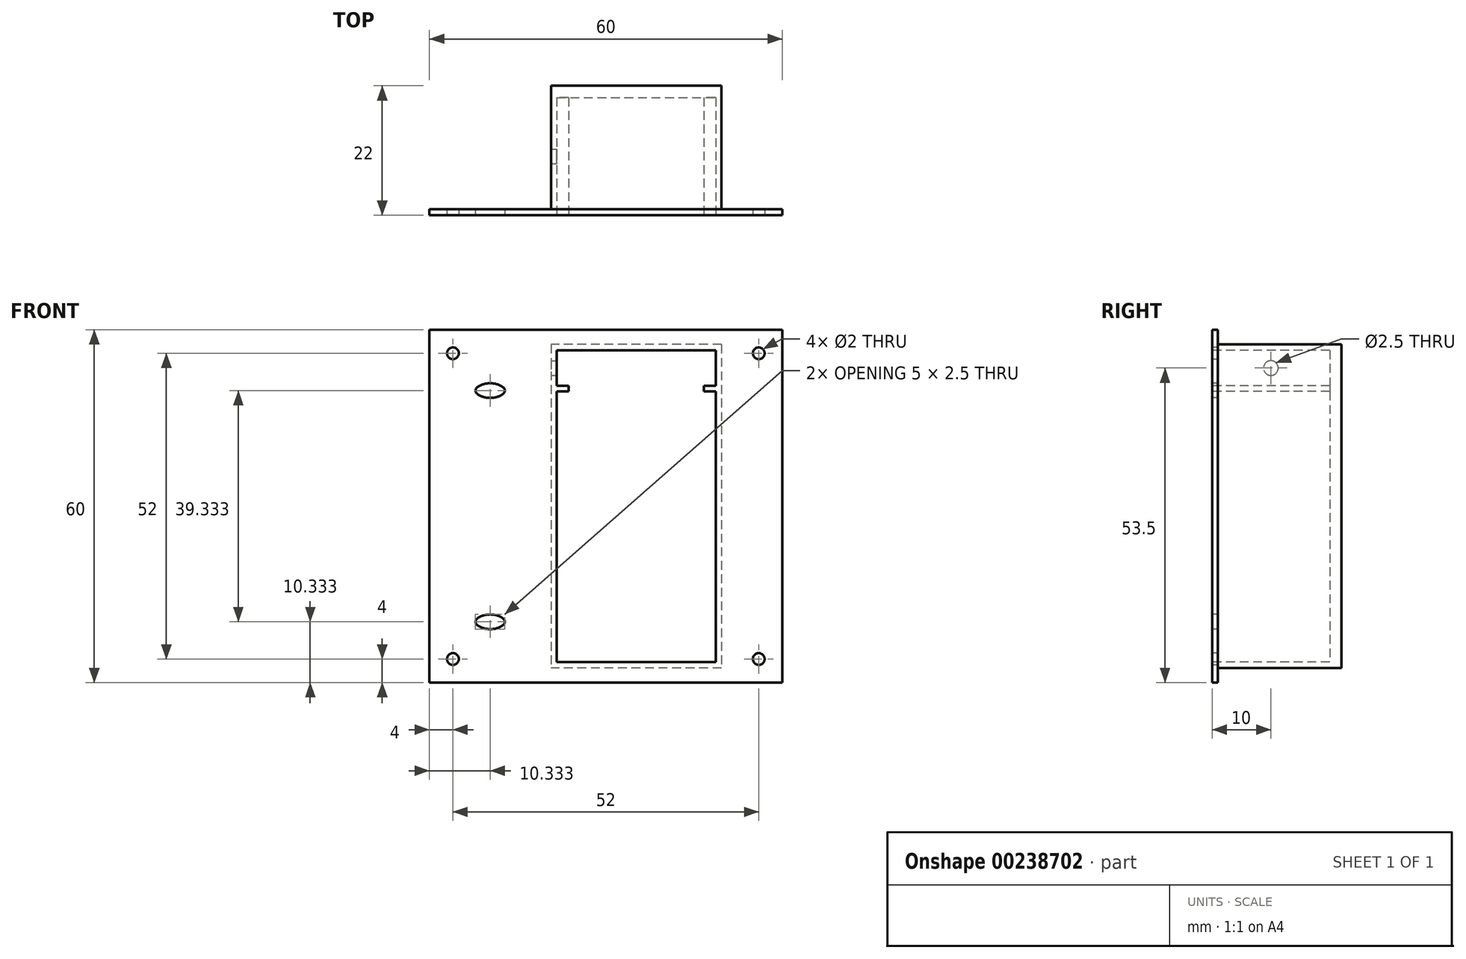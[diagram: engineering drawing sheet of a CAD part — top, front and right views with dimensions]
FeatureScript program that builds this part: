
annotation { "Feature Type Name" : "Feature", "Feature Type Description" : "" }
export const myFeature = defineFeature(function(context is Context, id is Id, definition is map)
    precondition{}
    {
        {
            var Q0;
            Q0=qCreatedBy(makeId("Front.planeOp"),FACE);
            var sketch = newSketch(context, id + "F0", { "sketchPlane" : qUnion([Q0])});
            skCircle(sketch, "E0", {"center": v(26.5, 16.25) * mm, "radius": 6.5 * mm, "construction": true});
            skCircle(sketch, "E1", {"center": v(45.5, 9.5) * mm, "radius": 4.5 * mm});
            skCircle(sketch, "E2", {"center": v(45.5, 9.5) * mm, "radius": 3 * mm});
            skCircle(sketch, "E3", {"center": v(45.5, 24.5) * mm, "radius": 3 * mm});
            skCircle(sketch, "E4", {"center": v(45.5, 24.5) * mm, "radius": 2.5 * mm});
            skLineSegment(sketch, "E5", {"start": v(45.5, 27.5) * mm, "end": v(45.5, 5) * mm, "construction": true});
            skPoint(sketch, "E6.positionSnap0", {"position": v(45.5, 16.25) * mm});
            skLineSegment(sketch, "E7.bottom", {"start": v(15, 32.5) * mm, "end": v(55, 32.5) * mm});
            skLineSegment(sketch, "E7.top", {"start": v(15, 0) * mm, "end": v(55, 0) * mm});
            skLineSegment(sketch, "E7.left", {"start": v(15, 32.5) * mm, "end": v(15, 0) * mm});
            skLineSegment(sketch, "E7.right", {"start": v(55, 32.5) * mm, "end": v(55, 0) * mm});
            skLineSegment(sketch, "E8", {"start": v(20.5, 22.25) * mm, "end": v(20.5, 23.75) * mm});
            skLineSegment(sketch, "E9", {"start": v(20.5, 23.75) * mm, "end": v(32.5, 23.75) * mm});
            skLineSegment(sketch, "E10", {"start": v(32.5, 23.75) * mm, "end": v(32.5, 22.25) * mm});
            skLineSegment(sketch, "E11", {"start": v(15, 16.25) * mm, "end": v(55, 16.25) * mm, "construction": true});
            skLineSegment(sketch, "E12.MirrorCS", {"start": v(32.5, 8.75) * mm, "end": v(32.5, 10.25) * mm});
            skLineSegment(sketch, "E13.MirrorCS", {"start": v(20.5, 8.75) * mm, "end": v(32.5, 8.75) * mm});
            skLineSegment(sketch, "E14.MirrorCS", {"start": v(20.5, 10.25) * mm, "end": v(20.5, 8.75) * mm});
            skLineSegment(sketch, "E15", {"start": v(50, 9.5) * mm, "end": v(55, 9.5) * mm, "construction": true});
            skLineSegment(sketch, "E16", {"start": v(41, 9.5) * mm, "end": v(41, 16.25) * mm, "construction": true});
            skLineSegment(sketch, "E17.bottom", {"start": v(32.5, 22.25) * mm, "end": v(20.5, 22.25) * mm});
            skLineSegment(sketch, "E17.top", {"start": v(32.5, 10.25) * mm, "end": v(20.5, 10.25) * mm});
            skLineSegment(sketch, "E17.left", {"start": v(32.5, 22.25) * mm, "end": v(32.5, 10.25) * mm});
            skLineSegment(sketch, "E17.right", {"start": v(20.5, 22.25) * mm, "end": v(20.5, 10.25) * mm});
            skLineSegment(sketch, "E18.bottom", {"start": v(24.5, 18.25) * mm, "end": v(28.5, 18.25) * mm});
            skLineSegment(sketch, "E18.top", {"start": v(24.5, 14.25) * mm, "end": v(28.5, 14.25) * mm});
            skLineSegment(sketch, "E18.left", {"start": v(24.5, 18.25) * mm, "end": v(24.5, 14.25) * mm});
            skLineSegment(sketch, "E18.right", {"start": v(28.5, 18.25) * mm, "end": v(28.5, 14.25) * mm});
            skLineSegment(sketch, "E19.1.0.0", {"start": v(92.5, 22.25) * mm, "end": v(80.5, 22.25) * mm});
            skCircle(sketch, "E19.1.0.1", {"center": v(105.5, 24.5) * mm, "radius": 2.5 * mm});
            skCircle(sketch, "E19.1.0.3", {"center": v(86.5, 16.25) * mm, "radius": 6.5 * mm, "construction": true});
            skLineSegment(sketch, "E19.1.0.4", {"start": v(115, 32.5) * mm, "end": v(115, 0) * mm});
            skLineSegment(sketch, "E19.1.0.5", {"start": v(75, 32.5) * mm, "end": v(115, 32.5) * mm});
            skLineSegment(sketch, "E19.1.0.6", {"start": v(84.5, 18.25) * mm, "end": v(84.5, 14.25) * mm});
            skLineSegment(sketch, "E19.1.0.7", {"start": v(84.5, 18.25) * mm, "end": v(88.5, 18.25) * mm});
            skLineSegment(sketch, "E19.1.0.8", {"start": v(92.5, 10.25) * mm, "end": v(80.5, 10.25) * mm});
            skLineSegment(sketch, "E19.1.0.9", {"start": v(80.5, 23.75) * mm, "end": v(92.5, 23.75) * mm});
            skCircle(sketch, "E19.1.0.10", {"center": v(105.5, 9.5) * mm, "radius": 4.5 * mm});
            skLineSegment(sketch, "E19.1.0.11", {"start": v(88.5, 18.25) * mm, "end": v(88.5, 14.25) * mm});
            skPoint(sketch, "E19.1.0.13", {"position": v(86.5, 16.25) * mm});
            skLineSegment(sketch, "E19.1.0.14", {"start": v(75, 32.5) * mm, "end": v(75, 0) * mm});
            skLineSegment(sketch, "E19.1.0.15", {"start": v(80.5, 8.75) * mm, "end": v(92.5, 8.75) * mm});
            skCircle(sketch, "E19.1.0.16", {"center": v(105.5, 9.5) * mm, "radius": 3 * mm});
            skCircle(sketch, "E19.1.0.17", {"center": v(105.5, 24.5) * mm, "radius": 3 * mm});
            skLineSegment(sketch, "E19.1.0.18", {"start": v(80.5, 22.25) * mm, "end": v(80.5, 10.25) * mm});
            skLineSegment(sketch, "E19.1.0.19", {"start": v(92.5, 22.25) * mm, "end": v(92.5, 10.25) * mm});
            skLineSegment(sketch, "E19.1.0.20", {"start": v(75, 0) * mm, "end": v(115, 0) * mm});
            skLineSegment(sketch, "E19.1.0.22", {"start": v(84.5, 14.25) * mm, "end": v(88.5, 14.25) * mm});
            skPoint(sketch, "E19.1.0.23", {"position": v(86.5, 16.25) * mm});
            skLineSegment(sketch, "E19.1.0.24", {"start": v(92.5, 23.75) * mm, "end": v(92.5, 22.25) * mm});
            skLineSegment(sketch, "E19.1.0.25", {"start": v(80.5, 22.25) * mm, "end": v(80.5, 23.75) * mm});
            skLineSegment(sketch, "E19.1.0.26", {"start": v(80.5, 10.25) * mm, "end": v(80.5, 8.75) * mm});
            skLineSegment(sketch, "E19.1.0.27", {"start": v(92.5, 8.75) * mm, "end": v(92.5, 10.25) * mm});
            skLineSegment(sketch, "E19.2.0.0", {"start": v(152.5, 22.25) * mm, "end": v(140.5, 22.25) * mm});
            skCircle(sketch, "E19.2.0.1", {"center": v(165.5, 24.5) * mm, "radius": 2.5 * mm});
            skCircle(sketch, "E19.2.0.3", {"center": v(146.5, 16.25) * mm, "radius": 6.5 * mm, "construction": true});
            skLineSegment(sketch, "E19.2.0.4", {"start": v(175, 32.5) * mm, "end": v(175, 0) * mm});
            skLineSegment(sketch, "E19.2.0.5", {"start": v(135, 32.5) * mm, "end": v(175, 32.5) * mm});
            skLineSegment(sketch, "E19.2.0.6", {"start": v(144.5, 18.25) * mm, "end": v(144.5, 14.25) * mm});
            skLineSegment(sketch, "E19.2.0.7", {"start": v(144.5, 18.25) * mm, "end": v(148.5, 18.25) * mm});
            skLineSegment(sketch, "E19.2.0.8", {"start": v(152.5, 10.25) * mm, "end": v(140.5, 10.25) * mm});
            skLineSegment(sketch, "E19.2.0.9", {"start": v(140.5, 23.75) * mm, "end": v(152.5, 23.75) * mm});
            skCircle(sketch, "E19.2.0.10", {"center": v(165.5, 9.5) * mm, "radius": 4.5 * mm});
            skLineSegment(sketch, "E19.2.0.11", {"start": v(148.5, 18.25) * mm, "end": v(148.5, 14.25) * mm});
            skPoint(sketch, "E19.2.0.13", {"position": v(146.5, 16.25) * mm});
            skLineSegment(sketch, "E19.2.0.14", {"start": v(135, 32.5) * mm, "end": v(135, 0) * mm});
            skLineSegment(sketch, "E19.2.0.15", {"start": v(140.5, 8.75) * mm, "end": v(152.5, 8.75) * mm});
            skCircle(sketch, "E19.2.0.16", {"center": v(165.5, 9.5) * mm, "radius": 3 * mm});
            skCircle(sketch, "E19.2.0.17", {"center": v(165.5, 24.5) * mm, "radius": 3 * mm});
            skLineSegment(sketch, "E19.2.0.18", {"start": v(140.5, 22.25) * mm, "end": v(140.5, 10.25) * mm});
            skLineSegment(sketch, "E19.2.0.19", {"start": v(152.5, 22.25) * mm, "end": v(152.5, 10.25) * mm});
            skLineSegment(sketch, "E19.2.0.20", {"start": v(135, 0) * mm, "end": v(175, 0) * mm});
            skLineSegment(sketch, "E19.2.0.22", {"start": v(144.5, 14.25) * mm, "end": v(148.5, 14.25) * mm});
            skPoint(sketch, "E19.2.0.23", {"position": v(146.5, 16.25) * mm});
            skLineSegment(sketch, "E19.2.0.24", {"start": v(152.5, 23.75) * mm, "end": v(152.5, 22.25) * mm});
            skLineSegment(sketch, "E19.2.0.25", {"start": v(140.5, 22.25) * mm, "end": v(140.5, 23.75) * mm});
            skLineSegment(sketch, "E19.2.0.26", {"start": v(140.5, 10.25) * mm, "end": v(140.5, 8.75) * mm});
            skLineSegment(sketch, "E19.2.0.27", {"start": v(152.5, 8.75) * mm, "end": v(152.5, 10.25) * mm});
            skLineSegment(sketch, "E19.3.0.0", {"start": v(212.5, 22.25) * mm, "end": v(200.5, 22.25) * mm});
            skCircle(sketch, "E19.3.0.1", {"center": v(225.5, 24.5) * mm, "radius": 2.5 * mm});
            skCircle(sketch, "E19.3.0.3", {"center": v(206.5, 16.25) * mm, "radius": 6.5 * mm, "construction": true});
            skLineSegment(sketch, "E19.3.0.4", {"start": v(235, 32.5) * mm, "end": v(235, 0) * mm});
            skLineSegment(sketch, "E19.3.0.5", {"start": v(195, 32.5) * mm, "end": v(235, 32.5) * mm});
            skLineSegment(sketch, "E19.3.0.6", {"start": v(204.5, 18.25) * mm, "end": v(204.5, 14.25) * mm});
            skLineSegment(sketch, "E19.3.0.7", {"start": v(204.5, 18.25) * mm, "end": v(208.5, 18.25) * mm});
            skLineSegment(sketch, "E19.3.0.8", {"start": v(212.5, 10.25) * mm, "end": v(200.5, 10.25) * mm});
            skLineSegment(sketch, "E19.3.0.9", {"start": v(200.5, 23.75) * mm, "end": v(212.5, 23.75) * mm});
            skCircle(sketch, "E19.3.0.10", {"center": v(225.5, 9.5) * mm, "radius": 4.5 * mm});
            skLineSegment(sketch, "E19.3.0.11", {"start": v(208.5, 18.25) * mm, "end": v(208.5, 14.25) * mm});
            skPoint(sketch, "E19.3.0.13", {"position": v(206.5, 16.25) * mm});
            skLineSegment(sketch, "E19.3.0.14", {"start": v(195, 32.5) * mm, "end": v(195, 0) * mm});
            skLineSegment(sketch, "E19.3.0.15", {"start": v(200.5, 8.75) * mm, "end": v(212.5, 8.75) * mm});
            skCircle(sketch, "E19.3.0.16", {"center": v(225.5, 9.5) * mm, "radius": 3 * mm});
            skCircle(sketch, "E19.3.0.17", {"center": v(225.5, 24.5) * mm, "radius": 3 * mm});
            skLineSegment(sketch, "E19.3.0.18", {"start": v(200.5, 22.25) * mm, "end": v(200.5, 10.25) * mm});
            skLineSegment(sketch, "E19.3.0.19", {"start": v(212.5, 22.25) * mm, "end": v(212.5, 10.25) * mm});
            skLineSegment(sketch, "E19.3.0.20", {"start": v(195, 0) * mm, "end": v(235, 0) * mm});
            skLineSegment(sketch, "E19.3.0.22", {"start": v(204.5, 14.25) * mm, "end": v(208.5, 14.25) * mm});
            skPoint(sketch, "E19.3.0.23", {"position": v(206.5, 16.25) * mm});
            skLineSegment(sketch, "E19.3.0.24", {"start": v(212.5, 23.75) * mm, "end": v(212.5, 22.25) * mm});
            skLineSegment(sketch, "E19.3.0.25", {"start": v(200.5, 22.25) * mm, "end": v(200.5, 23.75) * mm});
            skLineSegment(sketch, "E19.3.0.26", {"start": v(200.5, 10.25) * mm, "end": v(200.5, 8.75) * mm});
            skLineSegment(sketch, "E19.3.0.27", {"start": v(212.5, 8.75) * mm, "end": v(212.5, 10.25) * mm});
            skLineSegment(sketch, "E19.direction1", {"start": v(15, 0) * mm, "end": v(75, 0) * mm, "construction": true});
            skLineSegment(sketch, "E20.bottom", {"start": v(0, -92.5) * mm, "end": v(250, -92.5) * mm, "construction": true});
            skLineSegment(sketch, "E20.top", {"start": v(0, 47.5) * mm, "end": v(250, 47.5) * mm, "construction": true});
            skLineSegment(sketch, "E20.right", {"start": v(250, -92.5) * mm, "end": v(250, 47.5) * mm, "construction": true});
            skLineSegment(sketch, "E21", {"start": v(115, 0) * mm, "end": v(135, 0) * mm, "construction": true});
            skLineSegment(sketch, "E22.bottom", {"start": v(144.5, -39.17) * mm, "end": v(98.5, -39.17) * mm});
            skLineSegment(sketch, "E22.top", {"start": v(144.5, -66.17) * mm, "end": v(98.5, -66.17) * mm});
            skLineSegment(sketch, "E22.right", {"start": v(98.5, -39.17) * mm, "end": v(98.5, -66.17) * mm});
            skLineSegment(sketch, "E23.bottom", {"start": v(151.5, -39.17) * mm, "end": v(145.5, -39.17) * mm});
            skLineSegment(sketch, "E23.top", {"start": v(151.5, -66.17) * mm, "end": v(145.5, -66.17) * mm});
            skLineSegment(sketch, "E23.left", {"start": v(151.5, -39.17) * mm, "end": v(151.5, -66.17) * mm});
            skLineSegment(sketch, "E24.bottom", {"start": v(152.5, -67.17) * mm, "end": v(97.5, -67.17) * mm});
            skLineSegment(sketch, "E24.top", {"start": v(152.5, -38.17) * mm, "end": v(97.5, -38.17) * mm});
            skLineSegment(sketch, "E24.left", {"start": v(152.5, -67.17) * mm, "end": v(152.5, -38.17) * mm});
            skLineSegment(sketch, "E24.right", {"start": v(97.5, -67.17) * mm, "end": v(97.5, -38.17) * mm});
            skLineSegment(sketch, "E25", {"start": v(145.5, -64.17) * mm, "end": v(144.5, -64.17) * mm});
            skLineSegment(sketch, "E26", {"start": v(145.5, -41.17) * mm, "end": v(144.5, -41.17) * mm});
            skLineSegment(sketch, "E27", {"start": v(145.5, -66.17) * mm, "end": v(145.5, -64.17) * mm});
            skLineSegment(sketch, "E28", {"start": v(144.5, -66.17) * mm, "end": v(144.5, -64.17) * mm});
            skLineSegment(sketch, "E29", {"start": v(145.5, -41.17) * mm, "end": v(145.5, -39.17) * mm});
            skLineSegment(sketch, "E30", {"start": v(144.5, -41.17) * mm, "end": v(144.5, -39.17) * mm});
            skLineSegment(sketch, "E31.bottom", {"start": v(95, -77.5) * mm, "end": v(95, -17.5) * mm});
            skLineSegment(sketch, "E31.top", {"start": v(155, -77.5) * mm, "end": v(155, -17.5) * mm});
            skLineSegment(sketch, "E31.left", {"start": v(95, -77.5) * mm, "end": v(155, -77.5) * mm});
            skLineSegment(sketch, "E31.right", {"start": v(95, -17.5) * mm, "end": v(155, -17.5) * mm});
            skLineSegment(sketch, "E32", {"start": v(125, -38.17) * mm, "end": v(125, -17.5) * mm, "construction": true});
            skLineSegment(sketch, "E33", {"start": v(97.5, -67.17) * mm, "end": v(97.5, -77.5) * mm, "construction": true});
            skLineSegment(sketch, "E34", {"start": v(125, 0) * mm, "end": v(125, -92.5) * mm, "construction": true});
            skLineSegment(sketch, "E35.1.0.0", {"start": v(175, -77.5) * mm, "end": v(175, -17.5) * mm});
            skLineSegment(sketch, "E35.1.0.1", {"start": v(235, -77.5) * mm, "end": v(235, -17.5) * mm});
            skLineSegment(sketch, "E35.1.0.2", {"start": v(232.5, -67.17) * mm, "end": v(177.5, -67.17) * mm});
            skLineSegment(sketch, "E35.1.0.3", {"start": v(232.5, -67.17) * mm, "end": v(232.5, -38.17) * mm});
            skLineSegment(sketch, "E35.1.0.4", {"start": v(175, -17.5) * mm, "end": v(235, -17.5) * mm});
            skLineSegment(sketch, "E35.1.0.5", {"start": v(178.5, -39.17) * mm, "end": v(178.5, -66.17) * mm});
            skLineSegment(sketch, "E35.1.0.9", {"start": v(224.5, -66.17) * mm, "end": v(178.5, -66.17) * mm});
            skLineSegment(sketch, "E35.1.0.10", {"start": v(205, -38.17) * mm, "end": v(205, -17.5) * mm, "construction": true});
            skLineSegment(sketch, "E35.1.0.11", {"start": v(177.5, -67.17) * mm, "end": v(177.5, -77.5) * mm, "construction": true});
            skLineSegment(sketch, "E35.1.0.12", {"start": v(232.5, -38.17) * mm, "end": v(177.5, -38.17) * mm});
            skLineSegment(sketch, "E35.1.0.14", {"start": v(224.5, -39.17) * mm, "end": v(178.5, -39.17) * mm});
            skLineSegment(sketch, "E35.1.0.17", {"start": v(175, -77.5) * mm, "end": v(235, -77.5) * mm});
            skLineSegment(sketch, "E35.1.0.18", {"start": v(231.5, -39.17) * mm, "end": v(231.5, -66.17) * mm});
            skLineSegment(sketch, "E35.1.0.19", {"start": v(177.5, -67.17) * mm, "end": v(177.5, -38.17) * mm});
            skLineSegment(sketch, "E35.1.0.23", {"start": v(224.5, -41.17) * mm, "end": v(224.5, -39.17) * mm});
            skLineSegment(sketch, "E35.1.0.24", {"start": v(231.5, -39.17) * mm, "end": v(225.5, -39.17) * mm});
            skLineSegment(sketch, "E35.1.0.25", {"start": v(225.5, -41.17) * mm, "end": v(225.5, -39.17) * mm});
            skLineSegment(sketch, "E35.1.0.26", {"start": v(231.5, -66.17) * mm, "end": v(225.5, -66.17) * mm});
            skLineSegment(sketch, "E35.1.0.27", {"start": v(225.5, -66.17) * mm, "end": v(225.5, -64.17) * mm});
            skLineSegment(sketch, "E35.1.0.28", {"start": v(225.5, -41.17) * mm, "end": v(224.5, -41.17) * mm});
            skLineSegment(sketch, "E35.1.0.29", {"start": v(224.5, -66.17) * mm, "end": v(224.5, -64.17) * mm});
            skLineSegment(sketch, "E35.1.0.30", {"start": v(225.5, -64.17) * mm, "end": v(224.5, -64.17) * mm});
            skLineSegment(sketch, "E35.direction1", {"start": v(95, -77.5) * mm, "end": v(175, -77.5) * mm, "construction": true});
            skLineSegment(sketch, "E36.bottom", {"start": v(36.67, -28) * mm, "end": v(36.67, -74) * mm});
            skLineSegment(sketch, "E36.top", {"start": v(63.67, -28) * mm, "end": v(63.67, -74) * mm});
            skLineSegment(sketch, "E36.right", {"start": v(36.67, -74) * mm, "end": v(63.67, -74) * mm});
            skLineSegment(sketch, "E37.bottom", {"start": v(36.67, -21) * mm, "end": v(36.67, -27) * mm});
            skLineSegment(sketch, "E37.top", {"start": v(63.67, -21) * mm, "end": v(63.67, -27) * mm});
            skLineSegment(sketch, "E37.left", {"start": v(36.67, -21) * mm, "end": v(63.67, -21) * mm});
            skLineSegment(sketch, "E38.bottom", {"start": v(64.67, -20) * mm, "end": v(64.67, -75) * mm});
            skLineSegment(sketch, "E38.top", {"start": v(35.67, -20) * mm, "end": v(35.67, -75) * mm});
            skLineSegment(sketch, "E38.left", {"start": v(64.67, -20) * mm, "end": v(35.67, -20) * mm});
            skLineSegment(sketch, "E38.right", {"start": v(64.67, -75) * mm, "end": v(35.67, -75) * mm});
            skLineSegment(sketch, "E39", {"start": v(61.67, -27) * mm, "end": v(61.67, -28) * mm});
            skLineSegment(sketch, "E40", {"start": v(38.67, -27) * mm, "end": v(38.67, -28) * mm});
            skLineSegment(sketch, "E41", {"start": v(63.67, -27) * mm, "end": v(61.67, -27) * mm});
            skLineSegment(sketch, "E42", {"start": v(63.67, -28) * mm, "end": v(61.67, -28) * mm});
            skLineSegment(sketch, "E43", {"start": v(38.67, -27) * mm, "end": v(36.67, -27) * mm});
            skLineSegment(sketch, "E44", {"start": v(38.67, -28) * mm, "end": v(36.67, -28) * mm});
            skLineSegment(sketch, "E45.bottom", {"start": v(75, -77.5) * mm, "end": v(15, -77.5) * mm});
            skLineSegment(sketch, "E45.top", {"start": v(75, -17.5) * mm, "end": v(15, -17.5) * mm});
            skLineSegment(sketch, "E45.left", {"start": v(75, -77.5) * mm, "end": v(75, -17.5) * mm});
            skLineSegment(sketch, "E45.right", {"start": v(15, -77.5) * mm, "end": v(15, -17.5) * mm});
            skLineSegment(sketch, "E46", {"start": v(25.33, -29.08) * mm, "end": v(15, -29.08) * mm, "construction": true});
            skLineSegment(sketch, "E47", {"start": v(64.67, -29.08) * mm, "end": v(75, -29.08) * mm, "construction": true});
            skLineSegment(sketch, "E48", {"start": v(25.33, -29.08) * mm, "end": v(35.67, -29.08) * mm, "construction": true});
            skCircle(sketch, "E49", {"center": v(19, 28.5) * mm, "radius": 1 * mm});
            skCircle(sketch, "E50", {"center": v(51, 28.5) * mm, "radius": 1 * mm});
            skCircle(sketch, "E51", {"center": v(51, 4) * mm, "radius": 1 * mm});
            skCircle(sketch, "E52", {"center": v(19, 4) * mm, "radius": 1 * mm});
            skCircle(sketch, "E53", {"center": v(19, -21.5) * mm, "radius": 1 * mm});
            skCircle(sketch, "E54", {"center": v(71, -21.5) * mm, "radius": 1 * mm});
            skCircle(sketch, "E55", {"center": v(19, -73.5) * mm, "radius": 1 * mm});
            skCircle(sketch, "E56", {"center": v(71, -73.5) * mm, "radius": 1 * mm});
            skCircle(sketch, "E57.1.0.0", {"center": v(79, 28.5) * mm, "radius": 1 * mm});
            skCircle(sketch, "E57.1.0.1", {"center": v(79, 4) * mm, "radius": 1 * mm});
            skCircle(sketch, "E57.1.0.2", {"center": v(111, 4) * mm, "radius": 1 * mm});
            skCircle(sketch, "E57.1.0.3", {"center": v(111, 28.5) * mm, "radius": 1 * mm});
            skCircle(sketch, "E57.2.0.0", {"center": v(139, 28.5) * mm, "radius": 1 * mm});
            skCircle(sketch, "E57.2.0.1", {"center": v(139, 4) * mm, "radius": 1 * mm});
            skCircle(sketch, "E57.2.0.2", {"center": v(171, 4) * mm, "radius": 1 * mm});
            skCircle(sketch, "E57.2.0.3", {"center": v(171, 28.5) * mm, "radius": 1 * mm});
            skCircle(sketch, "E57.3.0.0", {"center": v(199, 28.5) * mm, "radius": 1 * mm});
            skCircle(sketch, "E57.3.0.1", {"center": v(199, 4) * mm, "radius": 1 * mm});
            skCircle(sketch, "E57.3.0.2", {"center": v(231, 4) * mm, "radius": 1 * mm});
            skCircle(sketch, "E57.3.0.3", {"center": v(231, 28.5) * mm, "radius": 1 * mm});
            skLineSegment(sketch, "E57.direction1", {"start": v(19, 4) * mm, "end": v(79, 4) * mm, "construction": true});
            skCircle(sketch, "E58.1.0.0", {"center": v(99, -73.5) * mm, "radius": 1 * mm});
            skCircle(sketch, "E58.1.0.1", {"center": v(151, -73.5) * mm, "radius": 1 * mm});
            skCircle(sketch, "E58.1.0.2", {"center": v(151, -21.5) * mm, "radius": 1 * mm});
            skCircle(sketch, "E58.1.0.3", {"center": v(99, -21.5) * mm, "radius": 1 * mm});
            skCircle(sketch, "E58.2.0.0", {"center": v(179, -73.5) * mm, "radius": 1 * mm});
            skCircle(sketch, "E58.2.0.1", {"center": v(231, -73.5) * mm, "radius": 1 * mm});
            skCircle(sketch, "E58.2.0.2", {"center": v(231, -21.5) * mm, "radius": 1 * mm});
            skCircle(sketch, "E58.2.0.3", {"center": v(179, -21.5) * mm, "radius": 1 * mm});
            skLineSegment(sketch, "E58.direction1", {"start": v(19, -73.5) * mm, "end": v(99, -73.5) * mm, "construction": true});
            skPoint(sketch, "E59.middle", {"position": v(25.33, -27.83) * mm});
            skLineSegment(sketch, "E60", {"start": v(15, -47.5) * mm, "end": v(35.67, -47.5) * mm, "construction": true});
            skPoint(sketch, "E61.1.0.0", {"position": v(112.5, -27.83) * mm});
            skLineSegment(sketch, "E62", {"start": v(112.5, -26.58) * mm, "end": v(112.5, -27.83) * mm, "construction": true});
            skLineSegment(sketch, "E63.bottom", {"start": v(115, -29.08) * mm, "end": v(110, -29.08) * mm, "construction": true});
            skLineSegment(sketch, "E63.top", {"start": v(115, -26.58) * mm, "end": v(110, -26.58) * mm, "construction": true});
            skLineSegment(sketch, "E63.left", {"start": v(115, -29.08) * mm, "end": v(115, -26.58) * mm, "construction": true});
            skLineSegment(sketch, "E63.right", {"start": v(110, -29.08) * mm, "end": v(110, -26.58) * mm, "construction": true});
            skFitSpline(sketch, "E64", {"points": [v(110, -27.83) * mm, v(110.5, -27.13) * mm, v(112.5, -26.58) * mm], "startDerivative": vector(0, 1.91) * mm, "endDerivative": vector(3.95, 0) * mm});
            skLineSegment(sketch, "E65", {"start": v(110, -27.83) * mm, "end": v(112.5, -27.83) * mm, "construction": true});
            skFitSpline(sketch, "E66.MirrorCS", {"points": [v(115, -27.83) * mm, v(114.5, -27.13) * mm, v(112.5, -26.58) * mm], "startDerivative": vector(0, 1.91) * mm, "endDerivative": vector(-3.95, 0) * mm});
            skFitSpline(sketch, "E67.MirrorCS", {"points": [v(110, -27.83) * mm, v(110.5, -28.53) * mm, v(112.5, -29.08) * mm], "startDerivative": vector(0, -1.91) * mm, "endDerivative": vector(3.95, 0) * mm});
            skFitSpline(sketch, "E68.MirrorCS", {"points": [v(115, -27.83) * mm, v(114.5, -28.53) * mm, v(112.5, -29.08) * mm], "startDerivative": vector(0, -1.91) * mm, "endDerivative": vector(-3.95, 0) * mm});
            skLineSegment(sketch, "E69", {"start": v(25.33, -17.5) * mm, "end": v(25.33, -27.83) * mm, "construction": true});
            skLineSegment(sketch, "E70.bottom", {"start": v(27.83, -29.08) * mm, "end": v(22.83, -29.08) * mm, "construction": true});
            skLineSegment(sketch, "E70.top", {"start": v(27.83, -26.58) * mm, "end": v(22.83, -26.58) * mm, "construction": true});
            skLineSegment(sketch, "E70.left", {"start": v(27.83, -29.08) * mm, "end": v(27.83, -26.58) * mm, "construction": true});
            skLineSegment(sketch, "E70.right", {"start": v(22.83, -29.08) * mm, "end": v(22.83, -26.58) * mm, "construction": true});
            skFitSpline(sketch, "E71", {"points": [v(22.83, -27.83) * mm, v(23.33, -27.13) * mm, v(25.33, -26.58) * mm], "startDerivative": vector(0, 1.91) * mm, "endDerivative": vector(3.95, 0) * mm});
            skLineSegment(sketch, "E72", {"start": v(22.83, -27.83) * mm, "end": v(25.33, -27.83) * mm, "construction": true});
            skFitSpline(sketch, "E73.MirrorCS", {"points": [v(27.83, -27.83) * mm, v(27.33, -27.13) * mm, v(25.33, -26.58) * mm], "startDerivative": vector(0, 1.91) * mm, "endDerivative": vector(-3.95, 0) * mm});
            skFitSpline(sketch, "E74.MirrorCS", {"points": [v(22.83, -27.83) * mm, v(23.33, -28.53) * mm, v(25.33, -29.08) * mm], "startDerivative": vector(0, -1.91) * mm, "endDerivative": vector(3.95, 0) * mm});
            skFitSpline(sketch, "E75.MirrorCS", {"points": [v(27.83, -27.83) * mm, v(27.33, -28.53) * mm, v(25.33, -29.08) * mm], "startDerivative": vector(0, -1.91) * mm, "endDerivative": vector(-3.95, 0) * mm});
            skFitSpline(sketch, "E76.MirrorCS", {"points": [v(135, -27.83) * mm, v(135.5, -27.13) * mm, v(137.5, -26.58) * mm], "startDerivative": vector(0, 1.91) * mm, "endDerivative": vector(3.95, 0) * mm});
            skFitSpline(sketch, "E77.MirrorCS", {"points": [v(135, -27.83) * mm, v(135.5, -28.53) * mm, v(137.5, -29.08) * mm], "startDerivative": vector(0, -1.91) * mm, "endDerivative": vector(3.95, 0) * mm});
            skFitSpline(sketch, "E78.MirrorCS", {"points": [v(140, -27.83) * mm, v(139.5, -28.53) * mm, v(137.5, -29.08) * mm], "startDerivative": vector(0, -1.91) * mm, "endDerivative": vector(-3.95, 0) * mm});
            skFitSpline(sketch, "E79.MirrorCS", {"points": [v(140, -27.83) * mm, v(139.5, -27.13) * mm, v(137.5, -26.58) * mm], "startDerivative": vector(0, 1.91) * mm, "endDerivative": vector(-3.95, 0) * mm});
            skPoint(sketch, "E80.MirrorP", {"position": v(137.5, -27.83) * mm});
            skFitSpline(sketch, "E81.MirrorCS", {"points": [v(27.83, -67.17) * mm, v(27.33, -66.47) * mm, v(25.33, -65.92) * mm], "startDerivative": vector(0, 1.91) * mm, "endDerivative": vector(-3.95, 0) * mm});
            skFitSpline(sketch, "E82.MirrorCS", {"points": [v(27.83, -67.17) * mm, v(27.33, -67.87) * mm, v(25.33, -68.42) * mm], "startDerivative": vector(0, -1.91) * mm, "endDerivative": vector(-3.95, 0) * mm});
            skFitSpline(sketch, "E83.MirrorCS", {"points": [v(22.83, -67.17) * mm, v(23.33, -67.87) * mm, v(25.33, -68.42) * mm], "startDerivative": vector(0, -1.91) * mm, "endDerivative": vector(3.95, 0) * mm});
            skFitSpline(sketch, "E84.MirrorCS", {"points": [v(22.83, -67.17) * mm, v(23.33, -66.47) * mm, v(25.33, -65.92) * mm], "startDerivative": vector(0, 1.91) * mm, "endDerivative": vector(3.95, 0) * mm});
            skPoint(sketch, "E85.1.0.0", {"position": v(192.5, -27.83) * mm});
            skLineSegment(sketch, "E86", {"start": v(192.5, -26.58) * mm, "end": v(192.5, -27.83) * mm, "construction": true});
            skLineSegment(sketch, "E87.bottom", {"start": v(195, -29.08) * mm, "end": v(190, -29.08) * mm, "construction": true});
            skLineSegment(sketch, "E87.top", {"start": v(195, -26.58) * mm, "end": v(190, -26.58) * mm, "construction": true});
            skLineSegment(sketch, "E87.left", {"start": v(195, -29.08) * mm, "end": v(195, -26.58) * mm, "construction": true});
            skLineSegment(sketch, "E87.right", {"start": v(190, -29.08) * mm, "end": v(190, -26.58) * mm, "construction": true});
            skFitSpline(sketch, "E88", {"points": [v(190, -27.83) * mm, v(190.5, -27.13) * mm, v(192.5, -26.58) * mm], "startDerivative": vector(0, 1.91) * mm, "endDerivative": vector(3.95, 0) * mm});
            skLineSegment(sketch, "E89", {"start": v(190, -27.83) * mm, "end": v(192.5, -27.83) * mm, "construction": true});
            skFitSpline(sketch, "E90.MirrorCS", {"points": [v(195, -27.83) * mm, v(194.5, -27.13) * mm, v(192.5, -26.58) * mm], "startDerivative": vector(0, 1.91) * mm, "endDerivative": vector(-3.95, 0) * mm});
            skFitSpline(sketch, "E91.MirrorCS", {"points": [v(190, -27.83) * mm, v(190.5, -28.53) * mm, v(192.5, -29.08) * mm], "startDerivative": vector(0, -1.91) * mm, "endDerivative": vector(3.95, 0) * mm});
            skFitSpline(sketch, "E92.MirrorCS", {"points": [v(195, -27.83) * mm, v(194.5, -28.53) * mm, v(192.5, -29.08) * mm], "startDerivative": vector(0, -1.91) * mm, "endDerivative": vector(-3.95, 0) * mm});
            skFitSpline(sketch, "E93.MirrorCS", {"points": [v(215, -27.83) * mm, v(215.5, -27.13) * mm, v(217.5, -26.58) * mm], "startDerivative": vector(0, 1.91) * mm, "endDerivative": vector(3.95, 0) * mm});
            skFitSpline(sketch, "E94.MirrorCS", {"points": [v(220, -27.83) * mm, v(219.5, -27.13) * mm, v(217.5, -26.58) * mm], "startDerivative": vector(0, 1.91) * mm, "endDerivative": vector(-3.95, 0) * mm});
            skFitSpline(sketch, "E95.MirrorCS", {"points": [v(220, -27.83) * mm, v(219.5, -28.53) * mm, v(217.5, -29.08) * mm], "startDerivative": vector(0, -1.91) * mm, "endDerivative": vector(-3.95, 0) * mm});
            skFitSpline(sketch, "E96.MirrorCS", {"points": [v(215, -27.83) * mm, v(215.5, -28.53) * mm, v(217.5, -29.08) * mm], "startDerivative": vector(0, -1.91) * mm, "endDerivative": vector(3.95, 0) * mm});
            skPoint(sketch, "E97.MirrorP", {"position": v(217.5, -27.83) * mm});
            skFitSpline(sketch, "E98.0", {"points": [v(28.33, -67.17) * mm, v(28.33, -67.33) * mm, v(28.25, -67.64) * mm, v(28, -67.98) * mm, v(27.67, -68.26) * mm, v(27.3, -68.48) * mm, v(26.86, -68.67) * mm, v(26.23, -68.85) * mm, v(25.7, -68.92) * mm, v(25.33, -68.92) * mm]});
            skFitSpline(sketch, "E98.1", {"points": [v(28.33, -67.17) * mm, v(28.33, -67) * mm, v(28.25, -66.7) * mm, v(28, -66.35) * mm, v(27.67, -66.08) * mm, v(27.3, -65.85) * mm, v(26.86, -65.67) * mm, v(26.23, -65.48) * mm, v(25.7, -65.42) * mm, v(25.33, -65.42) * mm]});
            skFitSpline(sketch, "E98.2", {"points": [v(22.33, -67.17) * mm, v(22.33, -67) * mm, v(22.42, -66.7) * mm, v(22.67, -66.35) * mm, v(23, -66.08) * mm, v(23.37, -65.85) * mm, v(23.8, -65.67) * mm, v(24.43, -65.48) * mm, v(24.97, -65.42) * mm, v(25.33, -65.42) * mm]});
            skFitSpline(sketch, "E98.3", {"points": [v(22.33, -67.17) * mm, v(22.33, -67.33) * mm, v(22.42, -67.64) * mm, v(22.67, -67.98) * mm, v(23, -68.26) * mm, v(23.37, -68.48) * mm, v(23.8, -68.67) * mm, v(24.43, -68.85) * mm, v(24.97, -68.92) * mm, v(25.33, -68.92) * mm]});
            skFitSpline(sketch, "E99.0", {"points": [v(28.33, -27.83) * mm, v(28.33, -28) * mm, v(28.25, -28.3) * mm, v(28, -28.65) * mm, v(27.67, -28.92) * mm, v(27.3, -29.15) * mm, v(26.86, -29.33) * mm, v(26.23, -29.52) * mm, v(25.7, -29.58) * mm, v(25.33, -29.58) * mm]});
            skFitSpline(sketch, "E99.1", {"points": [v(28.33, -27.83) * mm, v(28.33, -27.67) * mm, v(28.25, -27.36) * mm, v(28, -27.02) * mm, v(27.67, -26.74) * mm, v(27.3, -26.52) * mm, v(26.86, -26.33) * mm, v(26.23, -26.15) * mm, v(25.7, -26.08) * mm, v(25.33, -26.08) * mm]});
            skFitSpline(sketch, "E99.2", {"points": [v(22.33, -27.83) * mm, v(22.33, -27.67) * mm, v(22.42, -27.36) * mm, v(22.67, -27.02) * mm, v(23, -26.74) * mm, v(23.37, -26.52) * mm, v(23.8, -26.33) * mm, v(24.43, -26.15) * mm, v(24.97, -26.08) * mm, v(25.33, -26.08) * mm]});
            skFitSpline(sketch, "E99.3", {"points": [v(22.33, -27.83) * mm, v(22.33, -28) * mm, v(22.42, -28.3) * mm, v(22.67, -28.65) * mm, v(23, -28.92) * mm, v(23.37, -29.15) * mm, v(23.8, -29.33) * mm, v(24.43, -29.52) * mm, v(24.97, -29.58) * mm, v(25.33, -29.58) * mm]});
            skFitSpline(sketch, "E100.0", {"points": [v(115.5, -27.83) * mm, v(115.5, -28) * mm, v(115.42, -28.3) * mm, v(115.16, -28.65) * mm, v(114.84, -28.92) * mm, v(114.46, -29.15) * mm, v(114.03, -29.33) * mm, v(113.4, -29.52) * mm, v(112.87, -29.58) * mm, v(112.5, -29.58) * mm]});
            skFitSpline(sketch, "E100.1", {"points": [v(115.5, -27.83) * mm, v(115.5, -27.67) * mm, v(115.42, -27.36) * mm, v(115.16, -27.02) * mm, v(114.84, -26.74) * mm, v(114.46, -26.52) * mm, v(114.03, -26.33) * mm, v(113.4, -26.15) * mm, v(112.87, -26.08) * mm, v(112.5, -26.08) * mm]});
            skFitSpline(sketch, "E100.2", {"points": [v(109.5, -27.83) * mm, v(109.5, -27.67) * mm, v(109.58, -27.36) * mm, v(109.84, -27.02) * mm, v(110.16, -26.74) * mm, v(110.54, -26.52) * mm, v(110.97, -26.33) * mm, v(111.6, -26.15) * mm, v(112.13, -26.08) * mm, v(112.5, -26.08) * mm]});
            skFitSpline(sketch, "E100.3", {"points": [v(109.5, -27.83) * mm, v(109.5, -28) * mm, v(109.58, -28.3) * mm, v(109.84, -28.65) * mm, v(110.16, -28.92) * mm, v(110.54, -29.15) * mm, v(110.97, -29.33) * mm, v(111.6, -29.52) * mm, v(112.13, -29.58) * mm, v(112.5, -29.58) * mm]});
            skFitSpline(sketch, "E101.0", {"points": [v(195.5, -27.83) * mm, v(195.5, -27.67) * mm, v(195.42, -27.36) * mm, v(195.16, -27.02) * mm, v(194.84, -26.74) * mm, v(194.46, -26.52) * mm, v(194.03, -26.33) * mm, v(193.4, -26.15) * mm, v(192.87, -26.08) * mm, v(192.5, -26.08) * mm]});
            skFitSpline(sketch, "E101.1", {"points": [v(195.5, -27.83) * mm, v(195.5, -28) * mm, v(195.42, -28.3) * mm, v(195.16, -28.65) * mm, v(194.84, -28.92) * mm, v(194.46, -29.15) * mm, v(194.03, -29.33) * mm, v(193.4, -29.52) * mm, v(192.87, -29.58) * mm, v(192.5, -29.58) * mm]});
            skFitSpline(sketch, "E101.2", {"points": [v(189.5, -27.83) * mm, v(189.5, -28) * mm, v(189.58, -28.3) * mm, v(189.84, -28.65) * mm, v(190.16, -28.92) * mm, v(190.54, -29.15) * mm, v(190.97, -29.33) * mm, v(191.6, -29.52) * mm, v(192.13, -29.58) * mm, v(192.5, -29.58) * mm]});
            skFitSpline(sketch, "E101.3", {"points": [v(189.5, -27.83) * mm, v(189.5, -27.67) * mm, v(189.58, -27.36) * mm, v(189.84, -27.02) * mm, v(190.16, -26.74) * mm, v(190.54, -26.52) * mm, v(190.97, -26.33) * mm, v(191.6, -26.15) * mm, v(192.13, -26.08) * mm, v(192.5, -26.08) * mm]});
            skFitSpline(sketch, "E102.0", {"points": [v(134.5, -27.83) * mm, v(134.5, -28) * mm, v(134.58, -28.3) * mm, v(134.84, -28.65) * mm, v(135.16, -28.92) * mm, v(135.54, -29.15) * mm, v(135.97, -29.33) * mm, v(136.6, -29.52) * mm, v(137.13, -29.58) * mm, v(137.5, -29.58) * mm]});
            skFitSpline(sketch, "E102.1", {"points": [v(134.5, -27.83) * mm, v(134.5, -27.67) * mm, v(134.58, -27.36) * mm, v(134.84, -27.02) * mm, v(135.16, -26.74) * mm, v(135.54, -26.52) * mm, v(135.97, -26.33) * mm, v(136.6, -26.15) * mm, v(137.13, -26.08) * mm, v(137.5, -26.08) * mm]});
            skFitSpline(sketch, "E102.2", {"points": [v(140.5, -27.83) * mm, v(140.5, -27.67) * mm, v(140.42, -27.36) * mm, v(140.16, -27.02) * mm, v(139.84, -26.74) * mm, v(139.46, -26.52) * mm, v(139.03, -26.33) * mm, v(138.4, -26.15) * mm, v(137.87, -26.08) * mm, v(137.5, -26.08) * mm]});
            skFitSpline(sketch, "E102.3", {"points": [v(140.5, -27.83) * mm, v(140.5, -28) * mm, v(140.42, -28.3) * mm, v(140.16, -28.65) * mm, v(139.84, -28.92) * mm, v(139.46, -29.15) * mm, v(139.03, -29.33) * mm, v(138.4, -29.52) * mm, v(137.87, -29.58) * mm, v(137.5, -29.58) * mm]});
            skFitSpline(sketch, "E103.0", {"points": [v(220.5, -27.83) * mm, v(220.5, -28) * mm, v(220.42, -28.3) * mm, v(220.16, -28.65) * mm, v(219.84, -28.92) * mm, v(219.46, -29.15) * mm, v(219.03, -29.33) * mm, v(218.4, -29.52) * mm, v(217.87, -29.58) * mm, v(217.5, -29.58) * mm]});
            skFitSpline(sketch, "E103.1", {"points": [v(220.5, -27.83) * mm, v(220.5, -27.67) * mm, v(220.42, -27.36) * mm, v(220.16, -27.02) * mm, v(219.84, -26.74) * mm, v(219.46, -26.52) * mm, v(219.03, -26.33) * mm, v(218.4, -26.15) * mm, v(217.87, -26.08) * mm, v(217.5, -26.08) * mm]});
            skFitSpline(sketch, "E103.2", {"points": [v(214.5, -27.83) * mm, v(214.5, -27.67) * mm, v(214.58, -27.36) * mm, v(214.84, -27.02) * mm, v(215.16, -26.74) * mm, v(215.54, -26.52) * mm, v(215.97, -26.33) * mm, v(216.6, -26.15) * mm, v(217.13, -26.08) * mm, v(217.5, -26.08) * mm]});
            skFitSpline(sketch, "E103.3", {"points": [v(214.5, -27.83) * mm, v(214.5, -28) * mm, v(214.58, -28.3) * mm, v(214.84, -28.65) * mm, v(215.16, -28.92) * mm, v(215.54, -29.15) * mm, v(215.97, -29.33) * mm, v(216.6, -29.52) * mm, v(217.13, -29.58) * mm, v(217.5, -29.58) * mm]});
            skLineSegment(sketch, "E104.top", {"start": v(135, -102.5) * mm, "end": v(115, -102.5) * mm});
            skLineSegment(sketch, "E104.left", {"start": v(135, -92.5) * mm, "end": v(135, -102.5) * mm});
            skLineSegment(sketch, "E104.right", {"start": v(115, -92.5) * mm, "end": v(115, -102.5) * mm});
            skPoint(sketch, "E104.middle", {"position": v(125, -97.5) * mm});
            skLineSegment(sketch, "E105", {"start": v(135, -92.5) * mm, "end": v(155, -92.5) * mm});
            skLineSegment(sketch, "E106.1.0.0", {"start": v(155, -92.5) * mm, "end": v(155, -102.5) * mm});
            skLineSegment(sketch, "E106.1.0.1", {"start": v(175, -102.5) * mm, "end": v(155, -102.5) * mm});
            skLineSegment(sketch, "E106.1.0.2", {"start": v(175, -92.5) * mm, "end": v(175, -102.5) * mm});
            skLineSegment(sketch, "E106.1.0.3", {"start": v(175, -92.5) * mm, "end": v(195, -92.5) * mm});
            skLineSegment(sketch, "E106.2.0.0", {"start": v(195, -92.5) * mm, "end": v(195, -102.5) * mm});
            skLineSegment(sketch, "E106.2.0.1", {"start": v(215, -102.5) * mm, "end": v(195, -102.5) * mm});
            skLineSegment(sketch, "E106.2.0.2", {"start": v(215, -92.5) * mm, "end": v(215, -102.5) * mm});
            skLineSegment(sketch, "E106.2.0.3", {"start": v(215, -92.5) * mm, "end": v(235, -92.5) * mm});
            skLineSegment(sketch, "E106.direction1", {"start": v(115, -102.5) * mm, "end": v(155, -102.5) * mm, "construction": true});
            skLineSegment(sketch, "E107.0.3.0", {"start": v(235, -92.5) * mm, "end": v(235, -102.5) * mm});
            skLineSegment(sketch, "E108.MirrorCS", {"start": v(15, -92.5) * mm, "end": v(15, -102.5) * mm});
            skLineSegment(sketch, "E109.MirrorCS", {"start": v(35, -92.5) * mm, "end": v(35, -102.5) * mm});
            skLineSegment(sketch, "E110.MirrorCS", {"start": v(35, -102.5) * mm, "end": v(55, -102.5) * mm});
            skLineSegment(sketch, "E111.MirrorCS", {"start": v(55, -92.5) * mm, "end": v(55, -102.5) * mm});
            skLineSegment(sketch, "E112.MirrorCS", {"start": v(75, -92.5) * mm, "end": v(75, -102.5) * mm});
            skLineSegment(sketch, "E113.MirrorCS", {"start": v(75, -102.5) * mm, "end": v(95, -102.5) * mm});
            skLineSegment(sketch, "E114.MirrorCS", {"start": v(95, -92.5) * mm, "end": v(95, -102.5) * mm});
            skLineSegment(sketch, "E115.MirrorCS", {"start": v(35, -92.5) * mm, "end": v(15, -92.5) * mm});
            skLineSegment(sketch, "E116.MirrorCS", {"start": v(115, -92.5) * mm, "end": v(95, -92.5) * mm});
            skLineSegment(sketch, "E117.MirrorCS", {"start": v(75, -92.5) * mm, "end": v(55, -92.5) * mm});
            skLineSegment(sketch, "E118.bottom", {"start": v(250, -12.5) * mm, "end": v(260, -12.5) * mm});
            skLineSegment(sketch, "E118.top", {"start": v(250, -32.5) * mm, "end": v(260, -32.5) * mm});
            skLineSegment(sketch, "E118.right", {"start": v(260, -12.5) * mm, "end": v(260, -32.5) * mm});
            skPoint(sketch, "E118.middle", {"position": v(255, -22.5) * mm});
            skPoint(sketch, "E118.middle.positionSnap0", {"position": v(250, -22.5) * mm});
            skPoint(sketch, "E118.centerSnap0", {"position": v(250, -22.5) * mm});
            skLineSegment(sketch, "E119", {"start": v(250, -12.5) * mm, "end": v(250, 7.5) * mm});
            skLineSegment(sketch, "E120.0.1.0", {"start": v(250, 7.5) * mm, "end": v(260, 7.5) * mm});
            skLineSegment(sketch, "E120.0.1.1", {"start": v(260, 27.5) * mm, "end": v(260, 7.5) * mm});
            skLineSegment(sketch, "E120.0.1.2", {"start": v(250, 27.5) * mm, "end": v(260, 27.5) * mm});
            skLineSegment(sketch, "E120.0.1.3", {"start": v(250, 27.5) * mm, "end": v(250, 47.5) * mm});
            skLineSegment(sketch, "E120.0.2.0", {"start": v(250, 47.5) * mm, "end": v(260, 47.5) * mm});
            skLineSegment(sketch, "E120.direction1", {"start": v(250, -32.5) * mm, "end": v(275, -32.5) * mm, "construction": true});
            skLineSegment(sketch, "E120.direction2", {"start": v(250, -32.5) * mm, "end": v(250, 7.5) * mm, "construction": true});
            skLineSegment(sketch, "E121", {"start": v(255, -22.5) * mm, "end": v(250, -22.5) * mm, "construction": true});
            skLineSegment(sketch, "E122.MirrorCS", {"start": v(250, -32.5) * mm, "end": v(250, -52.5) * mm});
            skLineSegment(sketch, "E123.MirrorCS", {"start": v(250, -52.5) * mm, "end": v(260, -52.5) * mm});
            skLineSegment(sketch, "E124.MirrorCS", {"start": v(260, -72.5) * mm, "end": v(260, -52.5) * mm});
            skLineSegment(sketch, "E125.MirrorCS", {"start": v(250, -72.5) * mm, "end": v(260, -72.5) * mm});
            skLineSegment(sketch, "E126.MirrorCS", {"start": v(250, -72.5) * mm, "end": v(250, -92.5) * mm});
            skLineSegment(sketch, "E127.MirrorCS", {"start": v(250, -92.5) * mm, "end": v(260, -92.5) * mm});
            skLineSegment(sketch, "E128", {"start": v(235, -102.5) * mm, "end": v(260, -102.5) * mm});
            skLineSegment(sketch, "E129", {"start": v(260, -102.5) * mm, "end": v(260, -92.5) * mm});
            skLineSegment(sketch, "E130.MirrorCS", {"start": v(35, 47.5) * mm, "end": v(35, 57.5) * mm});
            skLineSegment(sketch, "E131.MirrorCS", {"start": v(115, 47.5) * mm, "end": v(115, 57.5) * mm});
            skLineSegment(sketch, "E132.MirrorCS", {"start": v(55, 47.5) * mm, "end": v(55, 57.5) * mm});
            skLineSegment(sketch, "E133.MirrorCS", {"start": v(155, 47.5) * mm, "end": v(155, 57.5) * mm});
            skLineSegment(sketch, "E134.MirrorCS", {"start": v(75, 47.5) * mm, "end": v(75, 57.5) * mm});
            skLineSegment(sketch, "E135.MirrorCS", {"start": v(235, 47.5) * mm, "end": v(235, 57.5) * mm});
            skLineSegment(sketch, "E136.MirrorCS", {"start": v(95, 47.5) * mm, "end": v(95, 57.5) * mm});
            skLineSegment(sketch, "E137.MirrorCS", {"start": v(15, 47.5) * mm, "end": v(15, 57.5) * mm});
            skLineSegment(sketch, "E138.MirrorCS", {"start": v(260, 57.5) * mm, "end": v(260, 47.5) * mm});
            skLineSegment(sketch, "E139.MirrorCS", {"start": v(175, 47.5) * mm, "end": v(175, 57.5) * mm});
            skLineSegment(sketch, "E140.MirrorCS", {"start": v(195, 47.5) * mm, "end": v(195, 57.5) * mm});
            skLineSegment(sketch, "E141.MirrorCS", {"start": v(135, 47.5) * mm, "end": v(135, 57.5) * mm});
            skLineSegment(sketch, "E142.MirrorCS", {"start": v(215, 47.5) * mm, "end": v(215, 57.5) * mm});
            skLineSegment(sketch, "E143.MirrorCS", {"start": v(135, 47.5) * mm, "end": v(155, 47.5) * mm});
            skLineSegment(sketch, "E144.MirrorCS", {"start": v(215, 47.5) * mm, "end": v(235, 47.5) * mm});
            skLineSegment(sketch, "E145.MirrorCS", {"start": v(175, 47.5) * mm, "end": v(195, 47.5) * mm});
            skLineSegment(sketch, "E146.MirrorCS", {"start": v(35, 47.5) * mm, "end": v(15, 47.5) * mm});
            skLineSegment(sketch, "E147.MirrorCS", {"start": v(115, 47.5) * mm, "end": v(95, 47.5) * mm});
            skLineSegment(sketch, "E148.MirrorCS", {"start": v(75, 47.5) * mm, "end": v(55, 47.5) * mm});
            skLineSegment(sketch, "E149.MirrorCS", {"start": v(135, 57.5) * mm, "end": v(115, 57.5) * mm});
            skLineSegment(sketch, "E150.MirrorCS", {"start": v(35, 57.5) * mm, "end": v(55, 57.5) * mm});
            skLineSegment(sketch, "E151.MirrorCS", {"start": v(175, 57.5) * mm, "end": v(155, 57.5) * mm});
            skLineSegment(sketch, "E152.MirrorCS", {"start": v(215, 57.5) * mm, "end": v(195, 57.5) * mm});
            skLineSegment(sketch, "E153.MirrorCS", {"start": v(75, 57.5) * mm, "end": v(95, 57.5) * mm});
            skLineSegment(sketch, "E154.MirrorCS", {"start": v(235, 57.5) * mm, "end": v(260, 57.5) * mm});
            skLineSegment(sketch, "E155.MirrorCS", {"start": v(15, -102.5) * mm, "end": v(-10, -102.5) * mm});
            skLineSegment(sketch, "E156.MirrorCS", {"start": v(-10, -102.5) * mm, "end": v(-10, -92.5) * mm});
            skLineSegment(sketch, "E157.MirrorCS", {"start": v(0, -92.5) * mm, "end": v(-10, -92.5) * mm});
            skLineSegment(sketch, "E158.MirrorCS", {"start": v(0, -72.5) * mm, "end": v(-10, -72.5) * mm});
            skLineSegment(sketch, "E159.MirrorCS", {"start": v(-10, -72.5) * mm, "end": v(-10, -52.5) * mm});
            skLineSegment(sketch, "E160.MirrorCS", {"start": v(0, -52.5) * mm, "end": v(-10, -52.5) * mm});
            skLineSegment(sketch, "E161.MirrorCS", {"start": v(0, -92.5) * mm, "end": v(0, 47.5) * mm, "construction": true});
            skLineSegment(sketch, "E162.MirrorCS", {"start": v(-10, -12.5) * mm, "end": v(-10, -32.5) * mm});
            skLineSegment(sketch, "E163.MirrorCS", {"start": v(0, -12.5) * mm, "end": v(-10, -12.5) * mm});
            skLineSegment(sketch, "E164.MirrorCS", {"start": v(0, 7.5) * mm, "end": v(-10, 7.5) * mm});
            skLineSegment(sketch, "E165.MirrorCS", {"start": v(-10, 27.5) * mm, "end": v(-10, 7.5) * mm});
            skLineSegment(sketch, "E166.MirrorCS", {"start": v(0, 27.5) * mm, "end": v(-10, 27.5) * mm});
            skLineSegment(sketch, "E167.MirrorCS", {"start": v(0, 47.5) * mm, "end": v(-10, 47.5) * mm});
            skLineSegment(sketch, "E168.MirrorCS", {"start": v(-10, 57.5) * mm, "end": v(-10, 47.5) * mm});
            skLineSegment(sketch, "E169.MirrorCS", {"start": v(0, 27.5) * mm, "end": v(0, 47.5) * mm});
            skLineSegment(sketch, "E170.MirrorCS", {"start": v(0, -12.5) * mm, "end": v(0, 7.5) * mm});
            skLineSegment(sketch, "E171.MirrorCS", {"start": v(0, -32.5) * mm, "end": v(0, -52.5) * mm});
            skLineSegment(sketch, "E172.MirrorCS", {"start": v(0, -72.5) * mm, "end": v(0, -92.5) * mm});
            skLineSegment(sketch, "E173.MirrorCS", {"start": v(0, -32.5) * mm, "end": v(-10, -32.5) * mm});
            skLineSegment(sketch, "E174", {"start": v(-10, 57.5) * mm, "end": v(15, 57.5) * mm});
            skSolve(sketch);
        }
        {
            var Q0;
            Q0=makeQuery(id+"F0.imprint","IMPRINT",FACE,{"disambiguationData":[TD([[makeQuery(id+"F0.imprint","IMPRINT",EDGE,{"derivedFrom":sQuery(id+"F0.wireOp",EDGE,"E38.bottom")}),1.0]])]});
            var Q1;
            Q1=makeQuery(id+"F0.imprint","IMPRINT",FACE,{"disambiguationData":[TD([[makeQuery(id+"F0.imprint","IMPRINT",EDGE,{"derivedFrom":sQuery(id+"F0.wireOp",EDGE,"E81.MirrorCS")}),-1.0]])]});
            var Q2;
            Q2=makeQuery(id+"F0.imprint","IMPRINT",FACE,{"disambiguationData":[TD([[makeQuery(id+"F0.imprint","IMPRINT",EDGE,{"derivedFrom":sQuery(id+"F0.wireOp",EDGE,"E71")}),1.0]])]});
            var Q3;
            Q3=makeQuery(id+"F0.imprint","IMPRINT",FACE,{"disambiguationData":[TD([[makeQuery(id+"F0.imprint","IMPRINT",EDGE,{"derivedFrom":sQuery(id+"F0.wireOp",EDGE,"E36.bottom")}),-1.0]])]});
            extrude(context, id + "F1", {"entities" : qUnion([Q0, Q1, Q2, Q3]), "oppositeDirection" : true, "depth" : 1 * mm});
        }
        {
            var Q0;
            Q0=makeQuery(id+"F0.imprint","IMPRINT",FACE,{"disambiguationData":[TD([[makeQuery(id+"F0.imprint","IMPRINT",EDGE,{"derivedFrom":sQuery(id+"F0.wireOp",EDGE,"E36.bottom")}),-1.0]])]});
            extrude(context, id + "F2", {"entities" : qUnion([Q0]), "operationType" : NewBodyOperationType.ADD, "oppositeDirection" : true, "depth" : 20 * mm});
        }
        {
            var Q0;
            Q0=makeQuery(id+"F2.opExtrude","CAP_FACE",FACE,{"disambiguationData":[OSD([sQuery(id+"F0.wireOp",EDGE,"E36.bottom"),sQuery(id+"F0.wireOp",EDGE,"E36.top"),sQuery(id+"F0.wireOp",EDGE,"E36.right"),sQuery(id+"F0.wireOp",EDGE,"E37.bottom"),sQuery(id+"F0.wireOp",EDGE,"E37.top"),sQuery(id+"F0.wireOp",EDGE,"E37.left"),sQuery(id+"F0.wireOp",EDGE,"E38.bottom"),sQuery(id+"F0.wireOp",EDGE,"E38.top"),sQuery(id+"F0.wireOp",EDGE,"E38.left"),sQuery(id+"F0.wireOp",EDGE,"E38.right"),sQuery(id+"F0.wireOp",EDGE,"E39"),sQuery(id+"F0.wireOp",EDGE,"E40"),sQuery(id+"F0.wireOp",EDGE,"E41"),sQuery(id+"F0.wireOp",EDGE,"E42"),sQuery(id+"F0.wireOp",EDGE,"E43"),sQuery(id+"F0.wireOp",EDGE,"E44")])],"isStart":false});
            var sketch = newSketch(context, id + "F3", { "sketchPlane" : qUnion([Q0])});
            skLineSegment(sketch, "E175.bottom", {"start": v(-64.67, -75) * mm, "end": v(-35.67, -75) * mm});
            skLineSegment(sketch, "E175.top", {"start": v(-64.67, -20) * mm, "end": v(-35.67, -20) * mm});
            skLineSegment(sketch, "E175.left", {"start": v(-64.67, -75) * mm, "end": v(-64.67, -20) * mm});
            skLineSegment(sketch, "E175.right", {"start": v(-35.67, -75) * mm, "end": v(-35.67, -20) * mm});
            skSolve(sketch);
        }
        {
            var Q0;
            Q0 = qSketchRegion(id + "F3", true);
            extrude(context, id + "F4", {"entities" : qUnion([Q0]), "operationType" : NewBodyOperationType.ADD, "depth" : 2 * mm});
        }
        {
            var Q0;
            {var subQ0=sQuery(id+"F0.wireOp",EDGE,"E37.bottom");Q0=makeQuery(id+"F2.boolean.opBoolean","MERGE",FACE,{"derivedFrom":[makeQuery(id+"F1.opExtrude","SWEPT_FACE",FACE,{"disambiguationData":[OSD([subQ0])]}),makeQuery(id+"F2.opExtrude","SWEPT_FACE",FACE,{"disambiguationData":[OSD([subQ0])]})]});}
            var sketch = newSketch(context, id + "F5", { "sketchPlane" : qUnion([Q0])});
            skCircle(sketch, "E176", {"center": v(10, -24) * mm, "radius": 1.25 * mm});
            skSolve(sketch);
        }
        {
            var Q0;
            Q0=makeQuery(id+"F5.imprint","IMPRINT",FACE,{"disambiguationData":[TD([[makeQuery(id+"F5.imprint","IMPRINT",EDGE,{"derivedFrom":sQuery(id+"F5.wireOp",EDGE,"E176")}),1.0]])]});
            var Q1;
            Q1=sQuery(id+"F5.wireOp",EDGE,"E176");
            var Q2;
            Q2=makeQuery(id+"F4.boolean.opBoolean","MERGE",FACE,{"derivedFrom":[makeQuery(id+"F2.opExtrude","SWEPT_FACE",FACE,{"disambiguationData":[OSD([sQuery(id+"F0.wireOp",EDGE,"E38.top")])]}),makeQuery(id+"F4.opExtrude","SWEPT_FACE",FACE,{"disambiguationData":[OSD([sQuery(id+"F3.wireOp",EDGE,"E175.right")])]})]});
            extrude(context, id + "F6", {"entities" : qUnion([Q0]), "operationType" : NewBodyOperationType.REMOVE, "surfaceEntities" : qUnion([Q1]), "endBound" : BoundingType.UP_TO_SURFACE, "oppositeDirection" : true, "endBoundEntityFace" : qUnion([Q2]), "depth" : 25 * mm});
        }
    });
